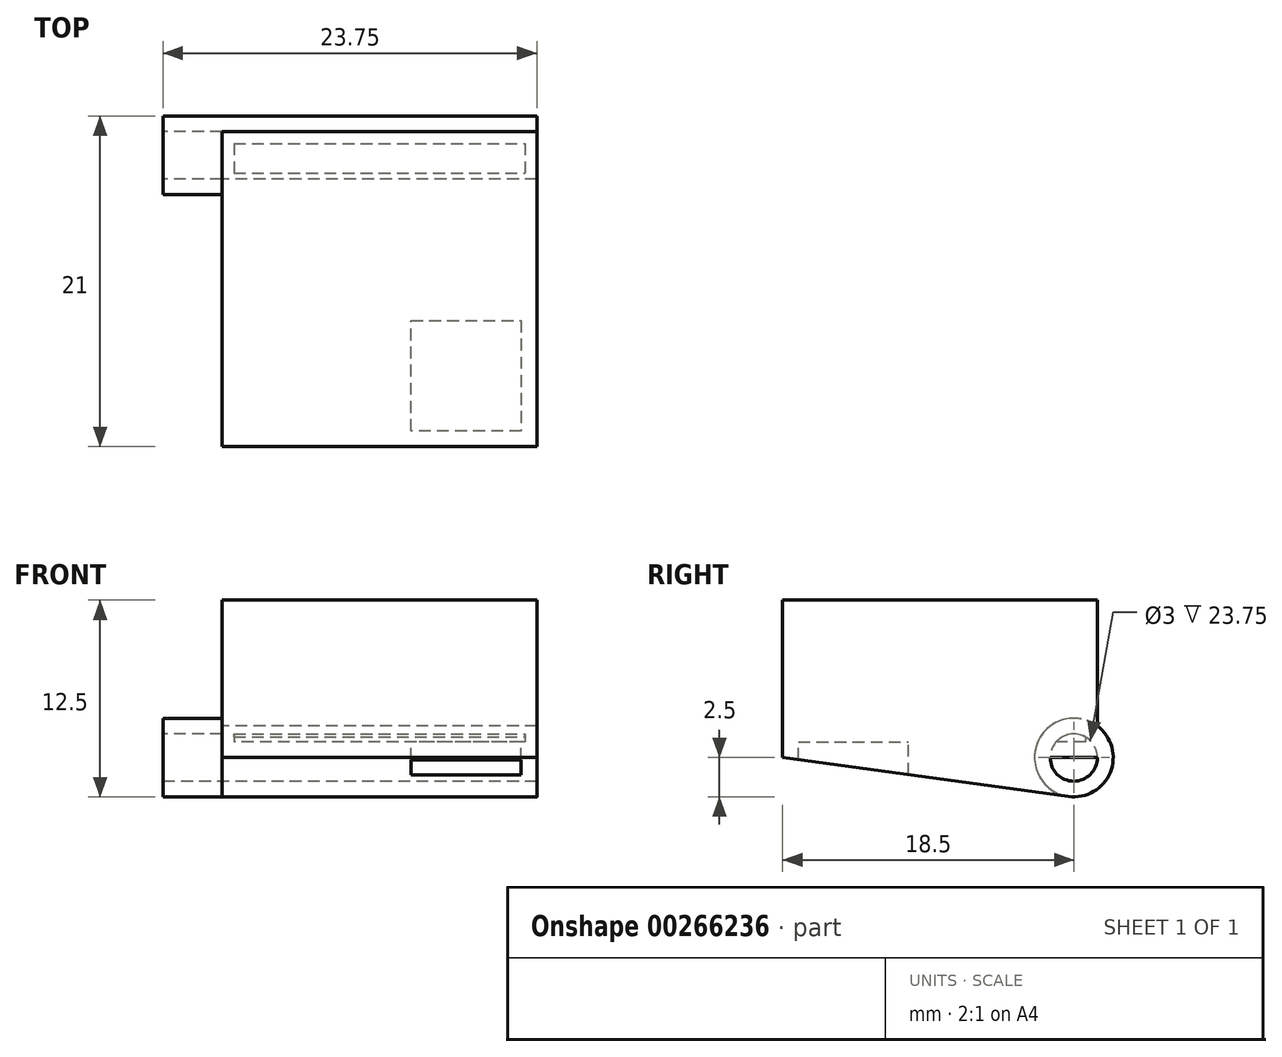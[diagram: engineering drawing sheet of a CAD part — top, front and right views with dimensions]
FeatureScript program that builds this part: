
annotation { "Feature Type Name" : "Feature", "Feature Type Description" : "" }
export const myFeature = defineFeature(function(context is Context, id is Id, definition is map)
    precondition{}
    {
        {
            var Q0;
            Q0=qCreatedBy(makeId("Top.planeOp"),FACE);
            var sketch = newSketch(context, id + "F0", { "sketchPlane" : qUnion([Q0])});
            skLineSegment(sketch, "E0.bottom", {"start": v(10, 10) * mm, "end": v(-10, 10) * mm});
            skLineSegment(sketch, "E0.top", {"start": v(10, -10) * mm, "end": v(-10, -10) * mm});
            skLineSegment(sketch, "E0.left", {"start": v(10, 10) * mm, "end": v(10, -10) * mm});
            skLineSegment(sketch, "E0.right", {"start": v(-10, 10) * mm, "end": v(-10, -10) * mm});
            skPoint(sketch, "E0.middle", {"position": v(0, 0) * mm});
            skLineSegment(sketch, "E1.bottom", {"start": v(9, -9) * mm, "end": v(2, -9) * mm});
            skLineSegment(sketch, "E1.top", {"start": v(9, -2) * mm, "end": v(2, -2) * mm});
            skLineSegment(sketch, "E1.left", {"start": v(9, -9) * mm, "end": v(9, -2) * mm});
            skLineSegment(sketch, "E1.right", {"start": v(2, -9) * mm, "end": v(2, -2) * mm});
            skPoint(sketch, "E1.middle", {"position": v(5.5, -5.5) * mm});
            skSolve(sketch);
        }
        {
            var Q0;
            Q0=makeQuery(id+"F0.imprint","IMPRINT",FACE,{"disambiguationData":[TD([[makeQuery(id+"F0.imprint","IMPRINT",EDGE,{"derivedFrom":sQuery(id+"F0.wireOp",EDGE,"E0.bottom")}),1.0]])]});
            extrude(context, id + "F1", {"entities" : qUnion([Q0]), "depth" : 1 * mm});
        }
        {
            var Q0;
            Q0=makeQuery(id+"F1.opExtrude","CAP_FACE",FACE,{"disambiguationData":[OSD([sQuery(id+"F0.wireOp",EDGE,"E0.bottom"),sQuery(id+"F0.wireOp",EDGE,"E0.top"),sQuery(id+"F0.wireOp",EDGE,"E0.left"),sQuery(id+"F0.wireOp",EDGE,"E0.right"),sQuery(id+"F0.wireOp",EDGE,"E1.bottom"),sQuery(id+"F0.wireOp",EDGE,"E1.top"),sQuery(id+"F0.wireOp",EDGE,"E1.left"),sQuery(id+"F0.wireOp",EDGE,"E1.right")])],"isStart":false});
            var sketch = newSketch(context, id + "F2", { "sketchPlane" : qUnion([Q0])});
            skLineSegment(sketch, "E2.bottom", {"start": v(9.25, 9.25) * mm, "end": v(-9.25, 9.25) * mm});
            skLineSegment(sketch, "E2.top", {"start": v(9.25, -9.25) * mm, "end": v(-9.25, -9.25) * mm});
            skLineSegment(sketch, "E2.left", {"start": v(9.25, 9.25) * mm, "end": v(9.25, -9.25) * mm});
            skLineSegment(sketch, "E2.right", {"start": v(-9.25, 9.25) * mm, "end": v(-9.25, -9.25) * mm});
            skPoint(sketch, "E2.middle", {"position": v(0, 0) * mm});
            skLineSegment(sketch, "E3.0", {"start": v(-10, 10) * mm, "end": v(-10, -10) * mm});
            skLineSegment(sketch, "E4.0", {"start": v(10, 10) * mm, "end": v(-10, 10) * mm});
            skLineSegment(sketch, "E5.0", {"start": v(10, -10) * mm, "end": v(-10, -10) * mm});
            skLineSegment(sketch, "E6.0", {"start": v(10, 10) * mm, "end": v(10, -10) * mm});
            skSolve(sketch);
        }
        {
            var Q0;
            Q0=makeQuery(id+"F2.imprint","IMPRINT",FACE,{"disambiguationData":[TD([[makeQuery(id+"F2.imprint","IMPRINT",EDGE,{"derivedFrom":sQuery(id+"F2.wireOp",EDGE,"E2.bottom")}),-1.0]])]});
            extrude(context, id + "F3", {"entities" : qUnion([Q0]), "operationType" : NewBodyOperationType.ADD, "depth" : 8.5 * mm});
        }
        {
            var Q0;
            Q0=makeQuery(id+"F3.opExtrude","CAP_FACE",FACE,{"disambiguationData":[OSD([sQuery(id+"F2.wireOp",EDGE,"E2.bottom"),sQuery(id+"F2.wireOp",EDGE,"E2.top"),sQuery(id+"F2.wireOp",EDGE,"E2.left"),sQuery(id+"F2.wireOp",EDGE,"E2.right"),sQuery(id+"F2.wireOp",EDGE,"E3.0"),sQuery(id+"F2.wireOp",EDGE,"E4.0"),sQuery(id+"F2.wireOp",EDGE,"E5.0"),sQuery(id+"F2.wireOp",EDGE,"E6.0")])],"isStart":false});
            var sketch = newSketch(context, id + "F4", { "sketchPlane" : qUnion([Q0])});
            skLineSegment(sketch, "E7.0.0", {"start": v(-10, -10) * mm, "end": v(10, -10) * mm});
            skLineSegment(sketch, "E7.0.1", {"start": v(10, -10) * mm, "end": v(10, 10) * mm});
            skLineSegment(sketch, "E7.0.2", {"start": v(10, 10) * mm, "end": v(-10, 10) * mm});
            skLineSegment(sketch, "E7.0.3", {"start": v(-10, 10) * mm, "end": v(-10, -10) * mm});
            skLineSegment(sketch, "E8.bottom", {"start": v(8.75, 8.75) * mm, "end": v(-8.75, 8.75) * mm});
            skLineSegment(sketch, "E8.top", {"start": v(8.75, -8.75) * mm, "end": v(-8.75, -8.75) * mm});
            skLineSegment(sketch, "E8.left", {"start": v(8.75, 8.75) * mm, "end": v(8.75, -8.75) * mm});
            skLineSegment(sketch, "E8.right", {"start": v(-8.75, 8.75) * mm, "end": v(-8.75, -8.75) * mm});
            skPoint(sketch, "E8.middle", {"position": v(0, 0) * mm});
            skSolve(sketch);
        }
        {
            var Q0;
            Q0=makeQuery(id+"F4.imprint","IMPRINT",FACE,{"disambiguationData":[TD([[makeQuery(id+"F4.imprint","IMPRINT",EDGE,{"derivedFrom":sQuery(id+"F4.wireOp",EDGE,"E8.bottom")}),-1.0]])]});
            var Q1;
            Q1=makeQuery(id+"F4.imprint","IMPRINT",FACE,{"disambiguationData":[TD([[makeQuery(id+"F4.imprint","IMPRINT",EDGE,{"derivedFrom":sQuery(id+"F4.wireOp",EDGE,"E7.0.0")}),-1.0]])]});
            extrude(context, id + "F5", {"entities" : qUnion([Q0, Q1]), "operationType" : NewBodyOperationType.ADD, "depth" : .5 * mm});
        }
        {
            var Q0;
            Q0=makeQuery(id+"F5.opExtrude","CAP_EDGE",EDGE,{"disambiguationData":[OSD([sQuery(id+"F4.wireOp",EDGE,"E8.bottom")])],"isStart":true});
            var Q1;
            Q1=makeQuery(id+"F5.opExtrude","CAP_EDGE",EDGE,{"disambiguationData":[OSD([sQuery(id+"F4.wireOp",EDGE,"E8.left")])],"isStart":true});
            var Q2;
            Q2=makeQuery(id+"F5.opExtrude","CAP_EDGE",EDGE,{"disambiguationData":[OSD([sQuery(id+"F4.wireOp",EDGE,"E8.right")])],"isStart":true});
            var Q3;
            Q3=makeQuery(id+"F5.opExtrude","CAP_EDGE",EDGE,{"disambiguationData":[OSD([sQuery(id+"F4.wireOp",EDGE,"E8.top")])],"isStart":true});
            chamfer(context, id + "F6", {"entities" : qUnion([Q0, Q1, Q2, Q3]), "chamferType" : ChamferType.TWO_OFFSETS, "width1" : .25 * mm, "oppositeDirection" : false, "width2" : .5 * mm, "tangentPropagation" : true});
        }
        {
            var Q0;
            Q0=makeQuery(id+"F5.boolean.opBoolean","MERGE",FACE,{"derivedFrom":[makeQuery(id+"F3.boolean.opBoolean","MERGE",FACE,{"derivedFrom":[makeQuery(id+"F1.opExtrude","SWEPT_FACE",FACE,{"disambiguationData":[OSD([sQuery(id+"F0.wireOp",EDGE,"E0.right")])]}),makeQuery(id+"F3.opExtrude","SWEPT_FACE",FACE,{"disambiguationData":[OSD([sQuery(id+"F2.wireOp",EDGE,"E3.0")])]})]}),makeQuery(id+"F5.opExtrude","SWEPT_FACE",FACE,{"disambiguationData":[OSD([sQuery(id+"F4.wireOp",EDGE,"E7.0.3")])]})]});
            var sketch = newSketch(context, id + "F7", { "sketchPlane" : qUnion([Q0])});
            skCircle(sketch, "E9", {"center": v(-8.5, 0) * mm, "radius": 1.5 * mm});
            skCircle(sketch, "E10", {"center": v(-8.5, 0) * mm, "radius": 2.5 * mm});
            skLineSegment(sketch, "E11", {"start": v(-8.16, -2.48) * mm, "end": v(10, 0) * mm});
            skLineSegment(sketch, "E12", {"start": v(10, 0) * mm, "end": v(-6, 0) * mm});
            skSolve(sketch);
        }
        {
            var Q0;
            {var subQ0=sQuery(id+"F7.wireOp",EDGE,"E10");var subQ8=makeQuery(id+"F7.imprint","INTERSECT",VERTEX,{"derivedFrom":[subQ0,sQuery(id+"F7.wireOp",EDGE,"E11")]});Q0=makeQuery(id+"F7.imprint","IMPRINT",FACE,{"disambiguationData":[TD([[makeQuery(id+"F7.imprint","IMPRINT",EDGE,{"disambiguationData":[TD([[subQ8,-1.0]])],"derivedFrom":subQ0}),1.0]])]});}
            var Q1;
            {var subQ0=sQuery(id+"F7.wireOp",EDGE,"E11");Q1=makeQuery(id+"F7.imprint","IMPRINT",FACE,{"disambiguationData":[TD([[makeQuery(id+"F7.imprint","IMPRINT",EDGE,{"derivedFrom":subQ0}),1.0]])]});}
            var Q2;
            Q2=makeQuery(id+"F5.boolean.opBoolean","MERGE",FACE,{"derivedFrom":[makeQuery(id+"F3.boolean.opBoolean","MERGE",FACE,{"derivedFrom":[makeQuery(id+"F1.opExtrude","SWEPT_FACE",FACE,{"disambiguationData":[OSD([sQuery(id+"F0.wireOp",EDGE,"E0.left")])]}),makeQuery(id+"F3.opExtrude","SWEPT_FACE",FACE,{"disambiguationData":[OSD([sQuery(id+"F2.wireOp",EDGE,"E6.0")])]})]}),makeQuery(id+"F5.opExtrude","SWEPT_FACE",FACE,{"disambiguationData":[OSD([sQuery(id+"F4.wireOp",EDGE,"E7.0.1")])]})]});
            extrude(context, id + "F8", {"entities" : qUnion([Q0, Q1]), "operationType" : NewBodyOperationType.ADD, "endBound" : BoundingType.UP_TO_SURFACE, "oppositeDirection" : true, "endBoundEntityFace" : qUnion([Q2]), "depth" : 5 * mm});
        }
        {
            var Q0;
            {var subQ0=sQuery(id+"F4.wireOp",EDGE,"E7.0.3");var subQ1=sQuery(id+"F2.wireOp",EDGE,"E3.0");var subQ2=sQuery(id+"F0.wireOp",EDGE,"E0.right");Q0=makeQuery(id+"F8.boolean.opBoolean","MERGE",FACE,{"derivedFrom":[makeQuery(id+"F5.boolean.opBoolean","MERGE",FACE,{"derivedFrom":[makeQuery(id+"F3.boolean.opBoolean","MERGE",FACE,{"derivedFrom":[makeQuery(id+"F1.opExtrude","SWEPT_FACE",FACE,{"disambiguationData":[OSD([subQ2])]}),makeQuery(id+"F3.opExtrude","SWEPT_FACE",FACE,{"disambiguationData":[OSD([subQ1])]})]}),makeQuery(id+"F5.opExtrude","SWEPT_FACE",FACE,{"disambiguationData":[OSD([subQ0])]})]}),makeQuery(id+"F8.opExtrude","CAP_FACE",FACE,{"disambiguationData":[OSD([sQuery(id+"F0.wireOp",EDGE,"E0.bottom"),subQ2,subQ1,sQuery(id+"F2.wireOp",EDGE,"E4.0"),sQuery(id+"F4.wireOp",EDGE,"E7.0.2"),subQ0,sQuery(id+"F7.wireOp",EDGE,"E9"),sQuery(id+"F7.wireOp",EDGE,"E10"),sQuery(id+"F7.wireOp",EDGE,"E11"),sQuery(id+"F7.wireOp",EDGE,"E12")])],"isStart":true})]});}
            var sketch = newSketch(context, id + "F9", { "sketchPlane" : qUnion([Q0])});
            skCircle(sketch, "E13", {"center": v(-8.5, 0) * mm, "radius": 1.5 * mm});
            skCircle(sketch, "E14", {"center": v(-8.5, 0) * mm, "radius": 2.5 * mm});
            skSolve(sketch);
        }
        {
            var Q0;
            {var subQ0=sQuery(id+"F9.wireOp",EDGE,"E13");var subQ1=sQuery(id+"F0.wireOp",EDGE,"E0.right");var subQ2=makeQuery(id+"F1.opExtrude","CAP_EDGE",EDGE,{"disambiguationData":[OSD([subQ1])],"isStart":true});var subQ3=makeQuery(id+"F9.imprint","INTERSECT",VERTEX,{"disambiguationData":[OD(0.0)],"derivedFrom":[subQ2,subQ0]});Q0=makeQuery(id+"F9.imprint","IMPRINT",FACE,{"disambiguationData":[TD([[makeQuery(id+"F9.imprint","IMPRINT",EDGE,{"disambiguationData":[TD([[subQ3,1.0]])],"derivedFrom":subQ0}),-1.0]])]});}
            extrude(context, id + "F10", {"entities" : qUnion([Q0]), "operationType" : NewBodyOperationType.ADD, "depth" : 3.75 * mm});
        }
        {
            var Q0;
            {var subQ0=sQuery(id+"F0.wireOp",EDGE,"E0.left");var subQ2=sQuery(id+"F4.wireOp",EDGE,"E7.0.1");var subQ3=sQuery(id+"F2.wireOp",EDGE,"E6.0");Q0=makeQuery(id+"FAOw9uxdWpIhgP2_1.1.F10.boolean.opBoolean","SPLIT",FACE,{"disambiguationData":[TD([makeQuery(id+"F8.opExtrude","SWEPT_FACE",FACE,{"disambiguationData":[OSD([sQuery(id+"F7.wireOp",EDGE,"E9")])]})])],"derivedFrom":makeQuery(id+"F8.boolean.opBoolean","MERGE",FACE,{"derivedFrom":[makeQuery(id+"F5.boolean.opBoolean","MERGE",FACE,{"derivedFrom":[makeQuery(id+"F3.boolean.opBoolean","MERGE",FACE,{"derivedFrom":[makeQuery(id+"F1.opExtrude","SWEPT_FACE",FACE,{"disambiguationData":[OSD([subQ0])]}),makeQuery(id+"F3.opExtrude","SWEPT_FACE",FACE,{"disambiguationData":[OSD([subQ3])]})]}),makeQuery(id+"F5.opExtrude","SWEPT_FACE",FACE,{"disambiguationData":[OSD([subQ2])]})]}),makeQuery(id+"F8.opExtrude","CAP_FACE",FACE,{"disambiguationData":[OSD([subQ0,subQ3,subQ2])],"isStart":false})]})});}
            var sketch = newSketch(context, id + "F11", { "sketchPlane" : qUnion([Q0])});
            skCircle(sketch, "E15", {"center": v(8.5, 0) * mm, "radius": 1.5 * mm});
            skSolve(sketch);
        }
        {
            var Q0;
            Q0=makeQuery(id+"F11.imprint","IMPRINT",FACE,{"disambiguationData":[TD([[makeQuery(id+"F11.imprint","IMPRINT",EDGE,{"disambiguationData":[OD(1.0)],"derivedFrom":sQuery(id+"F11.wireOp",EDGE,"E15")}),1.0]])]});
            var Q1;
            {var subQ0=sQuery(id+"F0.wireOp",EDGE,"E0.right");var subQ1=sQuery(id+"F0.wireOp",EDGE,"E0.bottom");var subQ2=sQuery(id+"F7.wireOp",EDGE,"E9");var subQ3=sQuery(id+"F4.wireOp",EDGE,"E7.0.3");var subQ4=sQuery(id+"F2.wireOp",EDGE,"E3.0");Q1=makeQuery(id+"F10.boolean.opBoolean","SPLIT",FACE,{"disambiguationData":[TD([makeQuery(id+"F8.opExtrude","SWEPT_FACE",FACE,{"disambiguationData":[OSD([subQ2])]})])],"derivedFrom":makeQuery(id+"F8.boolean.opBoolean","MERGE",FACE,{"derivedFrom":[makeQuery(id+"F5.boolean.opBoolean","MERGE",FACE,{"derivedFrom":[makeQuery(id+"F3.boolean.opBoolean","MERGE",FACE,{"derivedFrom":[makeQuery(id+"F1.opExtrude","SWEPT_FACE",FACE,{"disambiguationData":[OSD([subQ0])]}),makeQuery(id+"F3.opExtrude","SWEPT_FACE",FACE,{"disambiguationData":[OSD([subQ4])]})]}),makeQuery(id+"F5.opExtrude","SWEPT_FACE",FACE,{"disambiguationData":[OSD([subQ3])]})]}),makeQuery(id+"F8.opExtrude","CAP_FACE",FACE,{"disambiguationData":[OSD([subQ1,subQ0,subQ4,sQuery(id+"F2.wireOp",EDGE,"E4.0"),sQuery(id+"F4.wireOp",EDGE,"E7.0.2"),subQ3,subQ2,sQuery(id+"F7.wireOp",EDGE,"E10"),sQuery(id+"F7.wireOp",EDGE,"E11"),sQuery(id+"F7.wireOp",EDGE,"E12")])],"isStart":true})]})});}
            extrude(context, id + "F12", {"entities" : qUnion([Q0]), "operationType" : NewBodyOperationType.ADD, "endBound" : BoundingType.UP_TO_SURFACE, "oppositeDirection" : true, "endBoundEntityFace" : qUnion([Q1]), "depth" : 25 * mm});
        }
        {
            var Q0;
            Q0=makeQuery(id+"F1.opExtrude","CAP_FACE",FACE,{"disambiguationData":[OSD([sQuery(id+"F0.wireOp",EDGE,"E0.bottom"),sQuery(id+"F0.wireOp",EDGE,"E0.top"),sQuery(id+"F0.wireOp",EDGE,"E0.left"),sQuery(id+"F0.wireOp",EDGE,"E0.right"),sQuery(id+"F0.wireOp",EDGE,"E1.bottom"),sQuery(id+"F0.wireOp",EDGE,"E1.top"),sQuery(id+"F0.wireOp",EDGE,"E1.left"),sQuery(id+"F0.wireOp",EDGE,"E1.right")])],"isStart":false});
            var sketch = newSketch(context, id + "F13", { "sketchPlane" : qUnion([Q0])});
            skLineSegment(sketch, "E16.0.0", {"start": v(9, -2) * mm, "end": v(2, -2) * mm});
            skLineSegment(sketch, "E16.0.1", {"start": v(2, -2) * mm, "end": v(2, -9) * mm});
            skLineSegment(sketch, "E16.0.2", {"start": v(2, -9) * mm, "end": v(9, -9) * mm});
            skLineSegment(sketch, "E16.0.3", {"start": v(9, -9) * mm, "end": v(9, -2) * mm});
            skSolve(sketch);
        }
        {
            var Q0;
            Q0=makeQuery(id+"F13.imprint","IMPRINT",FACE,{"disambiguationData":[TD([[makeQuery(id+"F13.imprint","IMPRINT",EDGE,{"derivedFrom":sQuery(id+"F13.wireOp",EDGE,"E16.0.0")}),1.0]])]});
            extrude(context, id + "F14", {"entities" : qUnion([Q0]), "operationType" : NewBodyOperationType.REMOVE, "endBound" : BoundingType.THROUGH_ALL, "oppositeDirection" : true, "depth" : 25 * mm});
        }
    });
